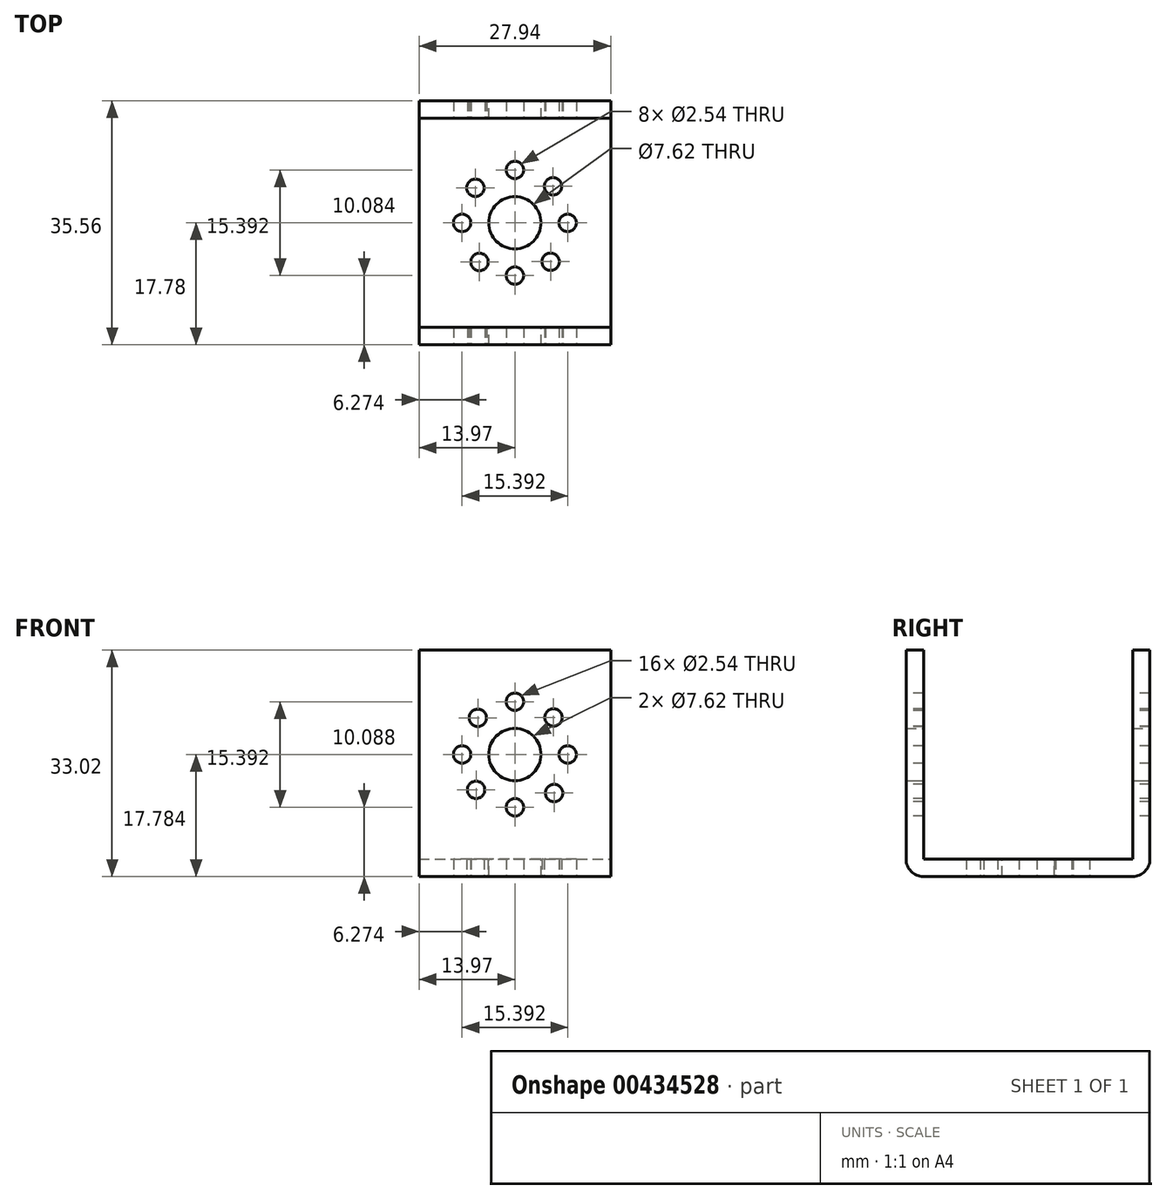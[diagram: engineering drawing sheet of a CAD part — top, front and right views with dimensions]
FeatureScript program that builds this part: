
annotation { "Feature Type Name" : "Feature", "Feature Type Description" : "" }
export const myFeature = defineFeature(function(context is Context, id is Id, definition is map)
    precondition{}
    {
        {
            var Q0;
            Q0=qCreatedBy(makeId("Front.planeOp"),FACE);
            var sketch = newSketch(context, id + "F0", { "sketchPlane" : qUnion([Q0])});
            skLineSegment(sketch, "E0.bottom", {"start": v(-13.97, 16.51) * mm, "end": v(13.97, 16.51) * mm});
            skLineSegment(sketch, "E0.top", {"start": v(-13.97, -16.51) * mm, "end": v(13.97, -16.51) * mm});
            skLineSegment(sketch, "E0.left", {"start": v(-13.97, 16.51) * mm, "end": v(-13.97, -16.51) * mm});
            skLineSegment(sketch, "E0.right", {"start": v(13.97, 16.51) * mm, "end": v(13.97, -16.51) * mm});
            skPoint(sketch, "E0.middle", {"position": v(0, 0) * mm});
            skSolve(sketch);
        }
        {
            var Q0;
            Q0=makeQuery(id+"F0.imprint","IMPRINT",FACE,{"disambiguationData":[TD([[makeQuery(id+"F0.imprint","IMPRINT",EDGE,{"derivedFrom":sQuery(id+"F0.wireOp",EDGE,"E0.bottom")}),-1.0]])]});
            extrude(context, id + "F1", {"entities" : qUnion([Q0]), "endBound" : BoundingType.SYMMETRIC, "depth" : 35.56 * mm});
        }
        {
            var Q0;
            Q0=makeQuery(id+"F1.opExtrude","SWEPT_FACE",FACE,{"disambiguationData":[OSD([sQuery(id+"F0.wireOp",EDGE,"E0.bottom")])]});
            var Q1;
            Q1=makeQuery(id+"F1.opExtrude","SWEPT_FACE",FACE,{"disambiguationData":[OSD([sQuery(id+"F0.wireOp",EDGE,"E0.left")])]});
            var Q2;
            Q2=makeQuery(id+"F1.opExtrude","SWEPT_FACE",FACE,{"disambiguationData":[OSD([sQuery(id+"F0.wireOp",EDGE,"E0.right")])]});
            shell(context, id + "F2", {"entities" : qUnion([Q0, Q1, Q2]), "thickness" : 2.54 * mm});
        }
        {
            var Q0;
            Q0=makeQuery(id+"F1.opExtrude","CAP_EDGE",EDGE,{"disambiguationData":[OSD([sQuery(id+"F0.wireOp",EDGE,"E0.top")])],"isStart":true});
            var Q1;
            Q1=makeQuery(id+"F1.opExtrude","CAP_EDGE",EDGE,{"disambiguationData":[OSD([sQuery(id+"F0.wireOp",EDGE,"E0.top")])],"isStart":false});
            fillet(context, id + "F3", {"entities" : qUnion([Q0, Q1]), "radius" : 2.54 * mm, "tangentPropagation" : true, "allowEdgeOverflow" : false});
        }
        {
            var Q0;
            Q0=makeQuery(id+"F2.opShell","OFFSET_FACE",FACE,{"disambiguationData":[OSD([sQuery(id+"F0.wireOp",EDGE,"E0.top")])]});
            var sketch = newSketch(context, id + "F4", { "sketchPlane" : qUnion([Q0])});
            skCircle(sketch, "E1", {"center": v(0, 0) * mm, "radius": 3.8 * mm});
            skSolve(sketch);
        }
        {
            var Q0;
            Q0=sQuery(id+"F4.wireOp",VERTEX,"E1.center");
            var Q1;
            Q1=makeQuery(id+"F1.opExtrude","SWEPT_BODY",BODY,{"disambiguationData":[OSD([sQuery(id+"F0.wireOp",EDGE,"E0.bottom"),sQuery(id+"F0.wireOp",EDGE,"E0.top"),sQuery(id+"F0.wireOp",EDGE,"E0.left"),sQuery(id+"F0.wireOp",EDGE,"E0.right")])]});
            hole(context, id + "F5", {"style" : HoleStyle.SIMPLE, "endStyle" : HoleEndStyle.THROUGH, "holeDiameter" : 7.62 * mm, "tappedDepth" : 12.7 * mm, "tapClearance" : 3, "locations" : qUnion([Q0]), "scope" : qUnion([Q1])});
        }
        {
            var Q0;
            Q0=makeQuery(id+"F1.opExtrude","CAP_FACE",FACE,{"disambiguationData":[OSD([sQuery(id+"F0.wireOp",EDGE,"E0.bottom"),sQuery(id+"F0.wireOp",EDGE,"E0.top"),sQuery(id+"F0.wireOp",EDGE,"E0.left"),sQuery(id+"F0.wireOp",EDGE,"E0.right")])],"isStart":true});
            var sketch = newSketch(context, id + "F6", { "sketchPlane" : qUnion([Q0])});
            skCircle(sketch, "E2", {"center": v(0, 1.27) * mm, "radius": 3.81 * mm});
            skSolve(sketch);
        }
        {
            var Q0;
            Q0=sQuery(id+"F6.wireOp",VERTEX,"qJwVwJcP-Efyk-cFFW-YqIM-0Mt75TvnPZuW.center");
            var Q1;
            Q1=sQuery(id+"F6.wireOp",VERTEX,"E2.center");
            var Q2;
            Q2=makeQuery(id+"F1.opExtrude","SWEPT_BODY",BODY,{"disambiguationData":[OSD([sQuery(id+"F0.wireOp",EDGE,"E0.bottom"),sQuery(id+"F0.wireOp",EDGE,"E0.top"),sQuery(id+"F0.wireOp",EDGE,"E0.left"),sQuery(id+"F0.wireOp",EDGE,"E0.right")])]});
            hole(context, id + "F7", {"style" : HoleStyle.SIMPLE, "endStyle" : HoleEndStyle.THROUGH, "holeDiameter" : 7.62 * mm, "tappedDepth" : 12.7 * mm, "tapClearance" : 3, "locations" : qUnion([Q0, Q1]), "scope" : qUnion([Q2])});
        }
        {
            var Q0;
            Q0=makeQuery(id+"F1.opExtrude","CAP_FACE",FACE,{"disambiguationData":[OSD([sQuery(id+"F0.wireOp",EDGE,"E0.bottom"),sQuery(id+"F0.wireOp",EDGE,"E0.top"),sQuery(id+"F0.wireOp",EDGE,"E0.left"),sQuery(id+"F0.wireOp",EDGE,"E0.right")])],"isStart":false});
            var sketch = newSketch(context, id + "F8", { "sketchPlane" : qUnion([Q0])});
            skCircle(sketch, "E3", {"center": v(0, 8.97) * mm, "radius": 1.27 * mm});
            skCircle(sketch, "E4", {"center": v(7.7, 1.27) * mm, "radius": 1.27 * mm});
            skCircle(sketch, "E5", {"center": v(0, -6.42) * mm, "radius": 1.27 * mm});
            skCircle(sketch, "E6", {"center": v(-5.4, 6.62) * mm, "radius": 1.27 * mm});
            skCircle(sketch, "E7", {"center": v(5.62, 6.67) * mm, "radius": 1.27 * mm});
            skCircle(sketch, "E8", {"center": v(5.72, -4.35) * mm, "radius": 1.27 * mm});
            skCircle(sketch, "E9", {"center": v(-5.66, -3.88) * mm, "radius": 1.27 * mm});
            skCircle(sketch, "E10", {"center": v(-7.7, 1.27) * mm, "radius": 1.27 * mm});
            skPoint(sketch, "E11.end.orphan", {"position": v(5.72, -3.88) * mm});
            skPoint(sketch, "E12.orphan", {"position": v(0, 1.27) * mm});
            skSolve(sketch);
        }
        {
            var Q0;
            Q0=sQuery(id+"F8.wireOp",VERTEX,"E6.center");
            var Q1;
            Q1=sQuery(id+"F8.wireOp",VERTEX,"E3.center");
            var Q2;
            Q2=sQuery(id+"F8.wireOp",VERTEX,"E7.center");
            var Q3;
            Q3=sQuery(id+"F8.wireOp",VERTEX,"E4.center");
            var Q4;
            Q4=sQuery(id+"F8.wireOp",VERTEX,"E8.center");
            var Q5;
            Q5=sQuery(id+"F8.wireOp",VERTEX,"E5.center");
            var Q6;
            Q6=sQuery(id+"F8.wireOp",VERTEX,"E9.center");
            var Q7;
            Q7=sQuery(id+"F8.wireOp",VERTEX,"7sUOdSip-NWSx-QvY7-50h7-tW5u177HJPZH.center");
            var Q8;
            Q8=sQuery(id+"F8.wireOp",VERTEX,"E10.center");
            var Q9;
            Q9=makeQuery(id+"F1.opExtrude","SWEPT_BODY",BODY,{"disambiguationData":[OSD([sQuery(id+"F0.wireOp",EDGE,"E0.bottom"),sQuery(id+"F0.wireOp",EDGE,"E0.top"),sQuery(id+"F0.wireOp",EDGE,"E0.left"),sQuery(id+"F0.wireOp",EDGE,"E0.right")])]});
            hole(context, id + "F9", {"style" : HoleStyle.SIMPLE, "endStyle" : HoleEndStyle.THROUGH, "holeDiameter" : 2.54 * mm, "tappedDepth" : 12.7 * mm, "tapClearance" : 3, "locations" : qUnion([Q0, Q1, Q2, Q3, Q4, Q5, Q6, Q7, Q8]), "scope" : qUnion([Q9])});
        }
        {
            var Q0;
            Q0=makeQuery(id+"F1.opExtrude","SWEPT_FACE",FACE,{"disambiguationData":[OSD([sQuery(id+"F0.wireOp",EDGE,"E0.top")])]});
            var sketch = newSketch(context, id + "F10", { "sketchPlane" : qUnion([Q0])});
            skCircle(sketch, "E13", {"center": v(0, 7.7) * mm, "radius": 1.27 * mm});
            skCircle(sketch, "E14", {"center": v(7.7, 0) * mm, "radius": 1.27 * mm});
            skCircle(sketch, "E15", {"center": v(0, -7.7) * mm, "radius": 1.27 * mm});
            skCircle(sketch, "E16", {"center": v(-7.7, 0) * mm, "radius": 1.27 * mm});
            skCircle(sketch, "E17", {"center": v(-5.16, 5.71) * mm, "radius": 1.27 * mm});
            skCircle(sketch, "E18", {"center": v(5.2, 5.67) * mm, "radius": 1.27 * mm});
            skCircle(sketch, "E19", {"center": v(5.56, -5.32) * mm, "radius": 1.27 * mm});
            skCircle(sketch, "E20", {"center": v(-5.76, -5.1) * mm, "radius": 1.27 * mm});
            skSolve(sketch);
        }
        {
            var Q0;
            Q0=sQuery(id+"F10.wireOp",VERTEX,"E17.center");
            var Q1;
            Q1=sQuery(id+"F10.wireOp",VERTEX,"E13.center");
            var Q2;
            Q2=sQuery(id+"F10.wireOp",VERTEX,"E18.center");
            var Q3;
            Q3=sQuery(id+"F10.wireOp",VERTEX,"E14.center");
            var Q4;
            Q4=sQuery(id+"F10.wireOp",VERTEX,"E20.center");
            var Q5;
            Q5=sQuery(id+"F10.wireOp",VERTEX,"E16.center");
            var Q6;
            Q6=sQuery(id+"F10.wireOp",VERTEX,"E15.center");
            var Q7;
            Q7=sQuery(id+"F10.wireOp",VERTEX,"E19.center");
            var Q8;
            Q8=makeQuery(id+"F1.opExtrude","SWEPT_BODY",BODY,{"disambiguationData":[OSD([sQuery(id+"F0.wireOp",EDGE,"E0.bottom"),sQuery(id+"F0.wireOp",EDGE,"E0.top"),sQuery(id+"F0.wireOp",EDGE,"E0.left"),sQuery(id+"F0.wireOp",EDGE,"E0.right")])]});
            hole(context, id + "F11", {"style" : HoleStyle.SIMPLE, "endStyle" : HoleEndStyle.THROUGH, "holeDiameter" : 2.54 * mm, "tappedDepth" : 12.7 * mm, "tapClearance" : 3, "locations" : qUnion([Q0, Q1, Q2, Q3, Q4, Q5, Q6, Q7]), "scope" : qUnion([Q8])});
        }
    });
